# Revit family: Einbaugeräte_Modul_45-Systeme_Steckdose_33°_Schutzkontakt_1_fach
name_source: partatom
category: Generic Models
revit_build: Autodesk Revit 2015 (Build: 20140606_1530(x64)
units: mm (PartAtom-declared; Revit-internal decimal feet)

## types (6) — shared parameters
Manufacturer = OBO Bettermann
URL = http://www.obo-bettermann.com

## per-type parameters (varying)
| type | GTIN | Manufacturer Art. No. | Material |
| STD-D3 MZGN1 | 4012196047505 | 6120076 | Polycarbonate, minzgrün |
| STD-D3 ROR1 | 4012196047468 | 6120074 | Polycarbonate, reinorange |
| STD-D3 RW1 | 4012196047444 | 6120072 | Polycarbonate, Clear reinweiß |
| STD-D3 SRO1 | 4012196047512 | 6120078 | Polycarbonate, signalrot |
| STD-D3 AL1 | 4012196047567 | 6120082 | Polycarbonate,Alu lackiert |
| STD-D3 SWGR1 | 4012196047529 | 6120080 | Polycarbonate, schwarzgrau |

note: column(s) folded — value = type name in every type: Article Type

## geometry (parser evidence)
native form markers: Sweep x2
no freeform markers — native parametric forms only
